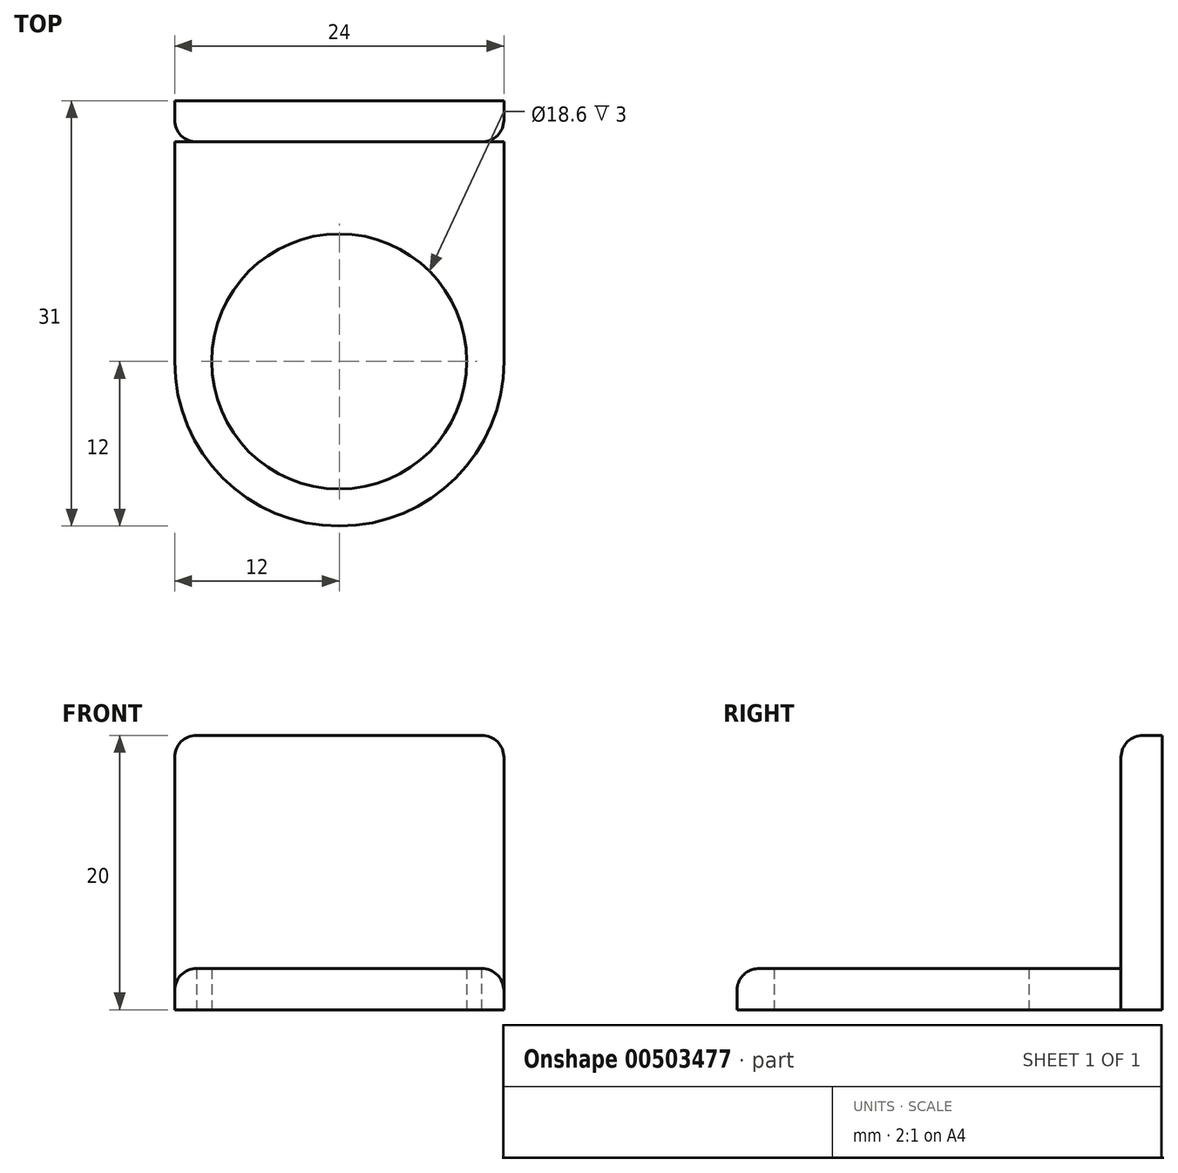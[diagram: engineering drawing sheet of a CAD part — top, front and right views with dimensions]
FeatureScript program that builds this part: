
annotation { "Feature Type Name" : "Feature", "Feature Type Description" : "" }
export const myFeature = defineFeature(function(context is Context, id is Id, definition is map)
    precondition{}
    {
        {
            var Q0;
            Q0=qCreatedBy(makeId("Top.planeOp"),FACE);
            var sketch = newSketch(context, id + "F0", { "sketchPlane" : qUnion([Q0])});
            skLineSegment(sketch, "E0", {"start": v(12, 0) * mm, "end": v(12, 16) * mm});
            skLineSegment(sketch, "E1", {"start": v(12, 16) * mm, "end": v(0, 16) * mm});
            skLineSegment(sketch, "E2", {"start": v(0, 16) * mm, "end": v(0, 9.3) * mm});
            skArc(sketch, "E3", {"start": v(0, -12) * mm, "mid": v(8.49, -8.49) * mm, "end": v(12, 0) * mm});
            skLineSegment(sketch, "E4", {"start": v(0, -12) * mm, "end": v(0, -9.3) * mm});
            skArc(sketch, "E5", {"start": v(0, 9.3) * mm, "mid": v(9.3, 0) * mm, "end": v(0, -9.3) * mm});
            skSolve(sketch);
        }
        {
            var Q0;
            Q0 = qSketchRegion(id + "F0", true);
            extrude(context, id + "F1", {"entities" : qUnion([Q0]), "depth" : 3 * mm, "offsetDistance" : 25 * mm});
        }
        {
            var Q0;
            Q0=makeQuery(id+"F1.opExtrude","SWEPT_BODY",BODY,{"disambiguationData":[OSD([sQuery(id+"F0.wireOp",EDGE,"E0"),sQuery(id+"F0.wireOp",EDGE,"E1"),sQuery(id+"F0.wireOp",EDGE,"E2"),sQuery(id+"F0.wireOp",EDGE,"E3"),sQuery(id+"F0.wireOp",EDGE,"E4"),sQuery(id+"F0.wireOp",EDGE,"E5")])]});
            var Q1;
            Q1=qCreatedBy(makeId("Right.planeOp"),FACE);
            mirror(context, id + "F2", {"operationType" : NewBodyOperationType.ADD, "entities" : qUnion([Q0]), "mirrorPlane" : qUnion([Q1])});
        }
        {
            var Q0;
            Q0=qCreatedBy(makeId("Front.planeOp"),FACE);
            var sketch = newSketch(context, id + "F3", { "sketchPlane" : qUnion([Q0])});
            skLineSegment(sketch, "E6", {"start": v(0, 0) * mm, "end": v(12, 0) * mm});
            skLineSegment(sketch, "E7", {"start": v(12, 0) * mm, "end": v(12, 20) * mm});
            skLineSegment(sketch, "E8", {"start": v(12, 20) * mm, "end": v(-12, 20) * mm});
            skLineSegment(sketch, "E9", {"start": v(-12, 20) * mm, "end": v(-12, 0) * mm});
            skLineSegment(sketch, "E10", {"start": v(-12, 0) * mm, "end": v(0, 0) * mm});
            skSolve(sketch);
        }
        {
            var Q0;
            Q0 = qSketchRegion(id + "F3", true);
            extrude(context, id + "F4", {"entities" : qUnion([Q0]), "depth" : 3 * mm, "offsetDistance" : 25 * mm});
        }
        {
            var Q0;
            Q0=makeQuery(id+"F4.opExtrude","SWEPT_BODY",BODY,{"disambiguationData":[OSD([sQuery(id+"F3.wireOp",EDGE,"E6"),sQuery(id+"F3.wireOp",EDGE,"E7"),sQuery(id+"F3.wireOp",EDGE,"E8"),sQuery(id+"F3.wireOp",EDGE,"E9"),sQuery(id+"F3.wireOp",EDGE,"E10")])]});
            transform(context, id + "F5", {"entities" : qUnion([Q0]), "transformType" : TransformType.TRANSLATION_3D, "dx" : 0 * mm, "dy" : 19 * mm, "dz" : 0 * mm, "makeCopy" : false});
        }
        {
            var Q0;
            Q0=makeQuery(id+"F4.opExtrude","CAP_EDGE",EDGE,{"disambiguationData":[OSD([sQuery(id+"F3.wireOp",EDGE,"E8")])],"isStart":false});
            var Q1;
            Q1=makeQuery(id+"F4.opExtrude","CAP_EDGE",EDGE,{"disambiguationData":[OSD([sQuery(id+"F3.wireOp",EDGE,"E9")])],"isStart":false});
            var Q2;
            Q2=makeQuery(id+"F4.opExtrude","CAP_EDGE",EDGE,{"disambiguationData":[OSD([sQuery(id+"F3.wireOp",EDGE,"E7")])],"isStart":false});
            var Q3;
            Q3=makeQuery(id+"F1.opExtrude","CAP_EDGE",EDGE,{"disambiguationData":[OSD([sQuery(id+"F0.wireOp",EDGE,"E0")])],"isStart":false});
            var Q4;
            Q4=makeQuery(id+"F4.opExtrude","SWEPT_EDGE",EDGE,{"disambiguationData":[OSD([sQuery(id+"F3.wireOp",EDGE,"E8"),sQuery(id+"F3.wireOp",EDGE,"E9")])]});
            var Q5;
            Q5=makeQuery(id+"F4.opExtrude","SWEPT_EDGE",EDGE,{"disambiguationData":[OSD([sQuery(id+"F3.wireOp",EDGE,"E7"),sQuery(id+"F3.wireOp",EDGE,"E8")])]});
            fillet(context, id + "F6", {"entities" : qUnion([Q0, Q1, Q2, Q3, Q4, Q5]), "radius" : 1.6 * mm, "tangentPropagation" : true, "allowEdgeOverflow" : false});
        }
    });
